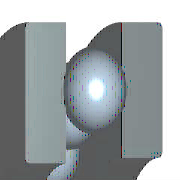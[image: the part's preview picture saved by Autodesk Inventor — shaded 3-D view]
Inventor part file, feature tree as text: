
AUTODESK INVENTOR PART (.ipt)
format: ipt  version: 2012 SP1 (Build 160190100, 190)  size: 187,392 bytes
history: native  units: mm (DEFAULTED — no unit token found)
features: chamfer x1
ambient origin geometry x8: Origin, YZ Plane, XZ Plane, XY Plane, X Axis, Y Axis, Z Axis, Center Point
bodies: Solid1 (feature_tree), Body (feature_tree)
feature tree (1):
  chamfer  "Chamfer1"  Distance=2.2mm
